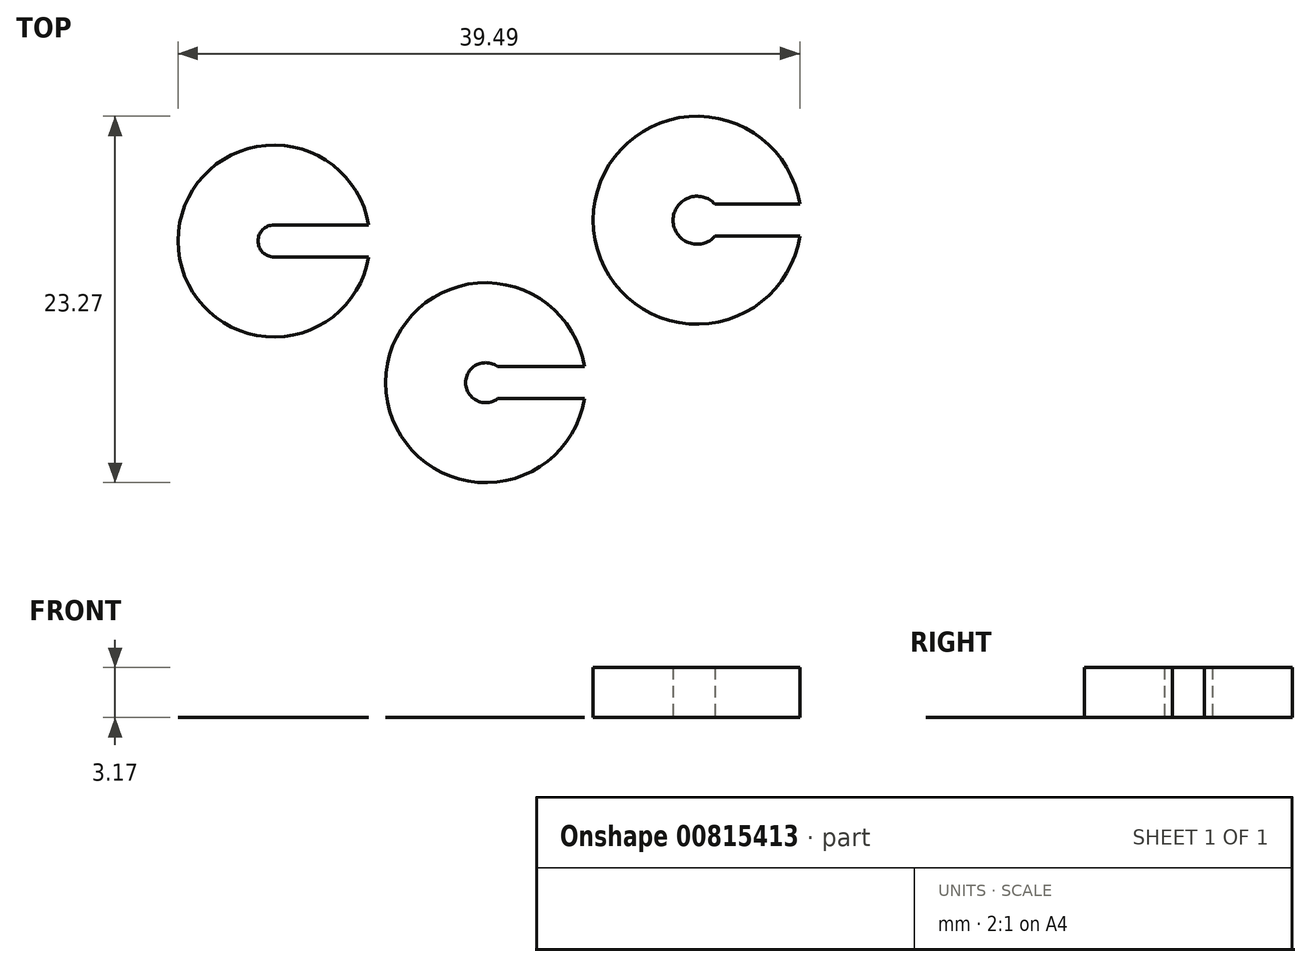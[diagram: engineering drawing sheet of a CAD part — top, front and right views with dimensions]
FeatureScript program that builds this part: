
annotation { "Feature Type Name" : "Feature", "Feature Type Description" : "" }
export const myFeature = defineFeature(function(context is Context, id is Id, definition is map)
    precondition{}
    {
        {
            var Q0;
            Q0=qCreatedBy(makeId("Top.planeOp"),FACE);
            var sketch = newSketch(context, id + "F0", { "sketchPlane" : qUnion([Q0])});
            skCircle(sketch, "E0", {"center": v(0, 0) * mm, "radius": 1.27 * mm});
            skCircle(sketch, "E1.0", {"center": v(0, 0) * mm, "radius": 6.35 * mm});
            skLineSegment(sketch, "E2", {"start": v(0.76, 1.02) * mm, "end": v(6.27, 1.02) * mm});
            skLineSegment(sketch, "E3", {"start": v(0.76, -1.02) * mm, "end": v(6.27, -1.02) * mm});
            skSolve(sketch);
        }
        {
            var Q0;
            {var subQ0=sQuery(id+"F0.wireOp",EDGE,"E2");Q0=makeQuery(id+"F0.imprint","IMPRINT",FACE,{"disambiguationData":[TD([[makeQuery(id+"F0.imprint","IMPRINT",EDGE,{"derivedFrom":subQ0}),1.0]])]});}
            extrude(context, id + "F1", {"entities" : qUnion([Q0]), "oppositeDirection" : true, "depth" : 1 / 203.2 * mm, "offsetDistance" : 25.4 * mm});
        }
        {
            var Q0;
            Q0=qCreatedBy(makeId("Top.planeOp"),FACE);
            var sketch = newSketch(context, id + "F2", { "sketchPlane" : qUnion([Q0])});
            skCircle(sketch, "E4", {"center": v(13.43, 10.32) * mm, "radius": 1.52 * mm});
            skCircle(sketch, "E5.0", {"center": v(13.43, 10.32) * mm, "radius": 6.6 * mm});
            skLineSegment(sketch, "E6", {"start": v(14.56, 11.34) * mm, "end": v(19.95, 11.34) * mm});
            skLineSegment(sketch, "E7", {"start": v(14.56, 9.3) * mm, "end": v(19.95, 9.3) * mm});
            skSolve(sketch);
        }
        {
            var Q0;
            {var subQ0=sQuery(id+"F2.wireOp",EDGE,"E6");Q0=makeQuery(id+"F2.imprint","IMPRINT",FACE,{"disambiguationData":[TD([[makeQuery(id+"F2.imprint","IMPRINT",EDGE,{"derivedFrom":subQ0}),1.0]])]});}
            extrude(context, id + "F3", {"entities" : qUnion([Q0]), "depth" : 3.17 * mm, "offsetDistance" : 25.4 * mm});
        }
        {
            var Q0;
            Q0=qCreatedBy(makeId("Top.planeOp"),FACE);
            var sketch = newSketch(context, id + "F4", { "sketchPlane" : qUnion([Q0])});
            skCircle(sketch, "E8", {"center": v(-13.44, 9) * mm, "radius": 1.02 * mm});
            skCircle(sketch, "E9.0", {"center": v(-13.44, 9) * mm, "radius": 6.1 * mm});
            skLineSegment(sketch, "E10", {"start": v(-13.44, 10.02) * mm, "end": v(-7.43, 10.02) * mm});
            skLineSegment(sketch, "E11", {"start": v(-13.44, 7.99) * mm, "end": v(-7.43, 7.99) * mm});
            skSolve(sketch);
        }
        {
            var Q0;
            {var subQ0=sQuery(id+"F4.wireOp",EDGE,"E10");Q0=makeQuery(id+"F4.imprint","IMPRINT",FACE,{"disambiguationData":[TD([[makeQuery(id+"F4.imprint","IMPRINT",EDGE,{"derivedFrom":subQ0}),1.0]])]});}
            extrude(context, id + "F5", {"entities" : qUnion([Q0]), "depth" : 1 / 203.2 * mm, "offsetDistance" : 25.4 * mm});
        }
    });
